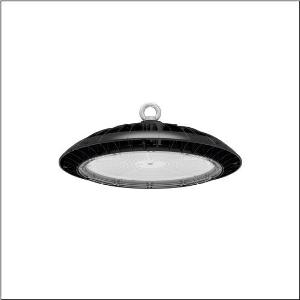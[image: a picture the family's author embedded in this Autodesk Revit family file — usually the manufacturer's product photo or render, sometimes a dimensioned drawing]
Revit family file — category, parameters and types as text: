
# Revit family: highbay_42-l_51hp32mb4mma
name_source: partatom
category: Lighting Fixtures
units: mm (PartAtom-declared; Revit-internal decimal feet)

## family parameters
Cut with Voids When Loaded = No
Host = Face
Light Source = No
Part Type = Normal
Room Calculation Point = No
Round Connector Dimension = Use Diameter
Shared = No

## types (1)
- --- (1 x LED, 28000 lm, 175 W, 4000K)
    Apparent Load = 175 VA
    CIE Flux Codes = 49 82 98 100 100
    Color Rendering = 80
    Color Temperature = 4000K
    Default Elevation = 1800 mm
    Description = Highbay 42-L, high bay luminaire, primary light control with lens, of PC, primary optical cover: cover panel, of PC, transparent, light emission: direct distribution, primary light characteristic: rotationally symmetric, installation type: suspended mounting, surface-mounted, LED, rated luminous flux: 28.000lm, luminous efficacy: 160lm/W, light colour: 840, colour temperature: 4000K, control gear: ON/OFF Multilumen, with cable, 3x 1.0mm², free wire ends, mains connection: 230V, AC, 50Hz, cable length: 1,5m, rated input power: 175W, housing, rotationally symmetric, of diecast aluminium, black, with hook on luminaire side, diameter: 305mm, height: 117mm, protection rating (complete): IP65, insulation class (complete): insulation class I (protective earthing), certification: CE, UKCA, protection symbol: D, impact resistance: IK08, permissible operating ambient temperature: -20..+40°C, corresponds to IFS (International Featured Standards) requirements for safety and quality in the food industry, packaging unit: 1 piece
    Height = 117 mm
    Lamp = 1 x LED
    Lamp Light Flux = 28000 lm
    Lamp Power = 175 W
    Lamp count = 1
    Length = 305 mm
    Luminous efficacy = 160 lm/W
    Manufacturer = Siteco
    ModVariant = No
    Model = 51HP32MB4MMA
    Mounting Place = Ceiling
    Mounting Type = Pendant
    Number of Poles = 1
    OnlyDefault = Yes
    Power Factor = 1
    Product Name = Highbay 42-L
    Product group = high bay luminaire
    ProductGroupID = 902
    Protection Class = Protection class I
    Protection Degree = IP 65
    RLX_Detail_Level = 1
    RLX_Emergency_Light_Flux = 0 lm
    RLX_Emergency_Type = 0
    RLX_Emergency_Type_DB = No
    RlxData = <blob elided: 286601 chars, md5=d7cc444b>
    Socket = socket
    Standby Power = 0 W
    System Light Flux = 28000 lm
    System Power = 175 W
    Type Comments = factory setting: luminous flux: 100 % | (OFF | OFF | OFF)
    Type Image = l_1003932.jpg
    URL = http://relux.com
    VarID = @adj_198747
    Voltage = 0 V
    Weight = 0.00 kg
    Width = 0 mm  [stored 0 ft]

note: [stored X ft] marks values corroborated as IEEE doubles in the binary element streams (Revit-internal decimal feet)

## geometry (parser evidence)
native form markers: Blend x4, Sweep x10
no freeform markers — native parametric forms only
